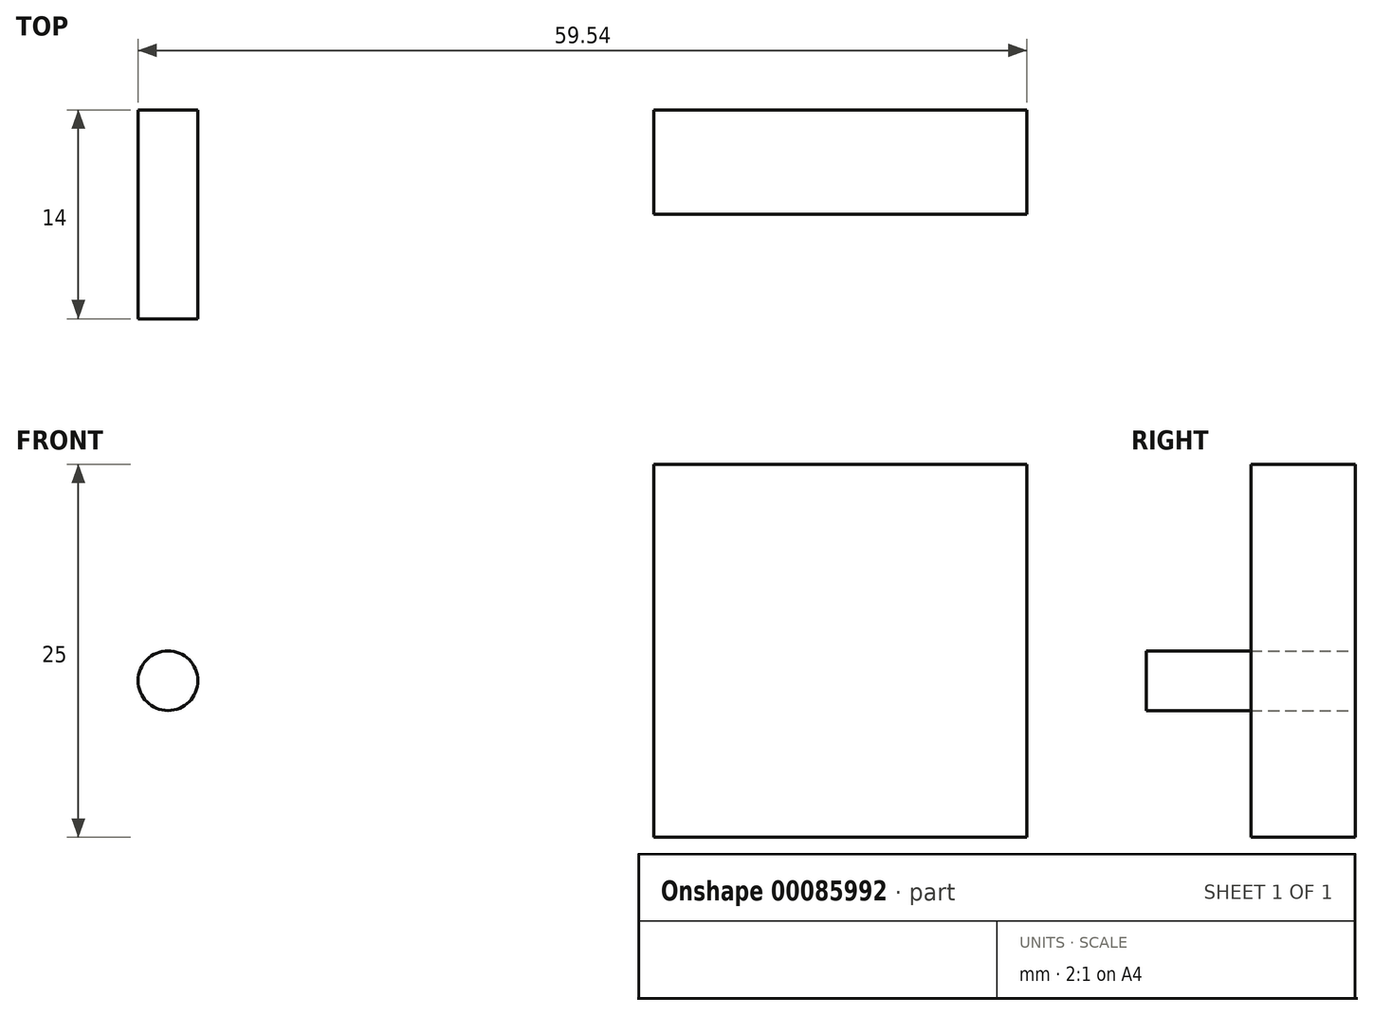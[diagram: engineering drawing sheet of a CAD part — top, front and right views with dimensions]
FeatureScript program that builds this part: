
annotation { "Feature Type Name" : "Feature", "Feature Type Description" : "" }
export const myFeature = defineFeature(function(context is Context, id is Id, definition is map)
    precondition{}
    {
        {
            var Q0;
            Q0=qCreatedBy(makeId("Front.planeOp"),FACE);
            var sketch = newSketch(context, id + "F0", { "sketchPlane" : qUnion([Q0])});
            skLineSegment(sketch, "E0.bottom", {"start": v(0, 0) * mm, "end": v(25, 0) * mm});
            skLineSegment(sketch, "E0.top", {"start": v(0, -25) * mm, "end": v(25, -25) * mm});
            skLineSegment(sketch, "E0.left", {"start": v(0, 0) * mm, "end": v(0, -25) * mm});
            skLineSegment(sketch, "E0.right", {"start": v(25, 0) * mm, "end": v(25, -25) * mm});
            skCircle(sketch, "E1", {"center": v(-32.54, -14.5) * mm, "radius": 2 * mm});
            skSolve(sketch);
        }
        {
            var Q0;
            Q0=makeQuery(id+"F0.imprint","IMPRINT",FACE,{"disambiguationData":[TD([[makeQuery(id+"F0.imprint","IMPRINT",EDGE,{"derivedFrom":sQuery(id+"F0.wireOp",EDGE,"E0.bottom")}),-1.0]])]});
            extrude(context, id + "F1", {"entities" : qUnion([Q0]), "depth" : 7 * mm});
        }
        {
            var Q0;
            Q0=makeQuery(id+"F0.imprint","IMPRINT",FACE,{"disambiguationData":[TD([[makeQuery(id+"F0.imprint","IMPRINT",EDGE,{"derivedFrom":sQuery(id+"F0.wireOp",EDGE,"E1")}),1.0]])]});
            extrude(context, id + "F2", {"entities" : qUnion([Q0]), "depth" : 14 * mm});
        }
    });
